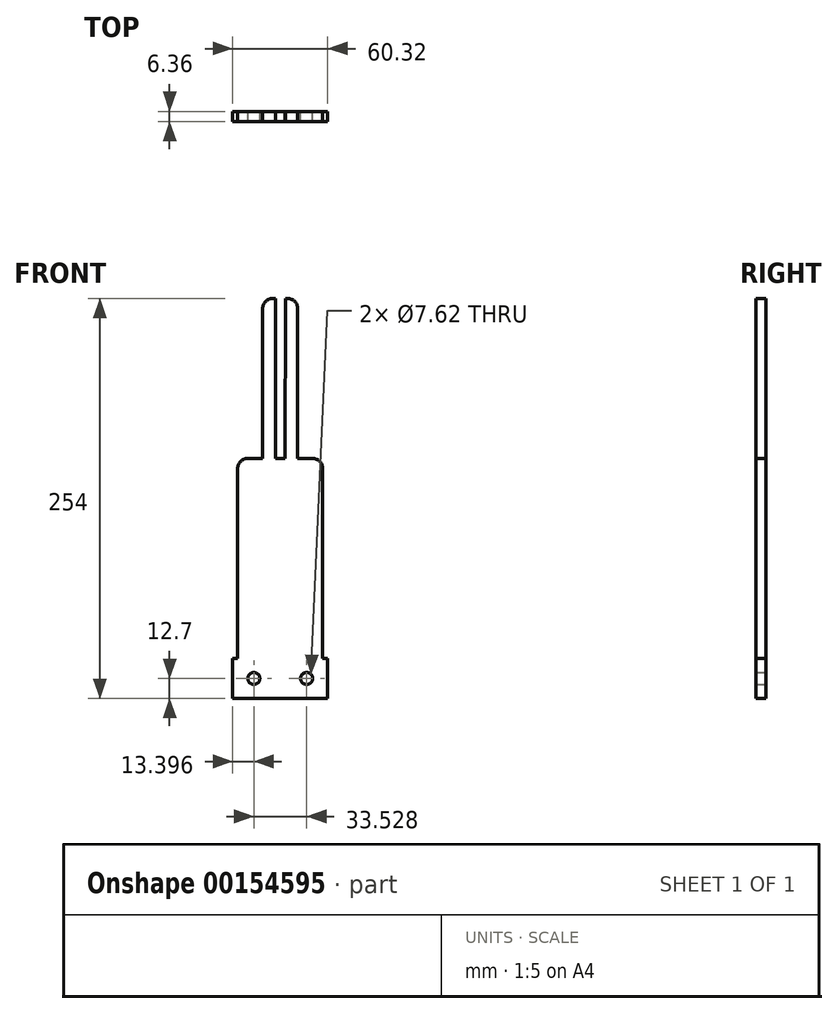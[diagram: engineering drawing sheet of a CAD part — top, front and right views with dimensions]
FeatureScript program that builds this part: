
annotation { "Feature Type Name" : "Feature", "Feature Type Description" : "" }
export const myFeature = defineFeature(function(context is Context, id is Id, definition is map)
    precondition{}
    {
        {
            var Q0;
            Q0=qCreatedBy(makeId("Front.planeOp"),FACE);
            var sketch = newSketch(context, id + "F0", { "sketchPlane" : qUnion([Q0])});
            skLineSegment(sketch, "E0.top", {"start": v(26.99, -12.7) * mm, "end": v(-26.99, -12.7) * mm});
            skLineSegment(sketch, "E0.left", {"start": v(26.99, 133.35) * mm, "end": v(26.99, 12.7) * mm});
            skLineSegment(sketch, "E0.right", {"start": v(-26.99, 133.35) * mm, "end": v(-26.99, 12.7) * mm});
            skPoint(sketch, "E0.middle", {"position": v(0, 0) * mm});
            skLineSegment(sketch, "E1", {"start": v(0, 0) * mm, "end": v(0, -12.7) * mm});
            skLineSegment(sketch, "E2", {"start": v(-20.64, 139.7) * mm, "end": v(-11.11, 139.7) * mm});
            skLineSegment(sketch, "E3", {"start": v(-4.76, 241.3) * mm, "end": v(-3.14, 241.3) * mm});
            skLineSegment(sketch, "E4", {"start": v(11.11, 234.95) * mm, "end": v(11.11, 139.7) * mm});
            skLineSegment(sketch, "E5.trimOffspring", {"start": v(-11.11, 139.7) * mm, "end": v(-11.11, 234.95) * mm});
            skLineSegment(sketch, "E6.trimOffspring", {"start": v(-3.14, 139.7) * mm, "end": v(3.17, 139.7) * mm});
            skLineSegment(sketch, "E7.trimOffspring", {"start": v(11.11, 139.7) * mm, "end": v(20.64, 139.7) * mm});
            skLineSegment(sketch, "E8", {"start": v(-3.14, 139.7) * mm, "end": v(-3.14, 241.3) * mm});
            skLineSegment(sketch, "E9", {"start": v(3.2, 241.3) * mm, "end": v(3.17, 139.7) * mm});
            skLineSegment(sketch, "E10.trimOffspring", {"start": v(3.2, 241.3) * mm, "end": v(4.76, 241.3) * mm});
            skPoint(sketch, "E11.visualSharp", {"position": v(-11.11, 241.3) * mm});
            skArc(sketch, "E11.filletArc", {"start": v(-4.76, 241.3) * mm, "mid": v(-9.25, 239.44) * mm, "end": v(-11.11, 234.95) * mm});
            skPoint(sketch, "E12.visualSharp", {"position": v(11.11, 241.3) * mm});
            skArc(sketch, "E12.filletArc", {"start": v(11.11, 234.95) * mm, "mid": v(9.25, 239.44) * mm, "end": v(4.76, 241.3) * mm});
            skCircle(sketch, "E13", {"center": v(-16.76, 0) * mm, "radius": 3.81 * mm});
            skCircle(sketch, "E14", {"center": v(16.76, 0) * mm, "radius": 3.81 * mm});
            skLineSegment(sketch, "E15", {"start": v(0, -12.7) * mm, "end": v(-3.17, -12.7) * mm});
            skLineSegment(sketch, "E16", {"start": v(-3.17, -12.7) * mm, "end": v(-3.17, 14.57) * mm, "construction": true});
            skLineSegment(sketch, "E17.MirrorCS", {"start": v(3.17, -12.7) * mm, "end": v(3.17, 14.57) * mm, "construction": true});
            skPoint(sketch, "E18.orphan", {"position": v(-26.99, 12.7) * mm});
            skPoint(sketch, "E19.orphan", {"position": v(26.99, 12.7) * mm});
            skLineSegment(sketch, "E20", {"start": v(-26.99, 12.7) * mm, "end": v(-30.16, 12.7) * mm});
            skLineSegment(sketch, "E21", {"start": v(-30.16, 12.7) * mm, "end": v(-30.16, -12.7) * mm});
            skLineSegment(sketch, "E22", {"start": v(-30.16, -12.7) * mm, "end": v(-26.99, -12.7) * mm});
            skLineSegment(sketch, "E23", {"start": v(26.99, -12.7) * mm, "end": v(30.16, -12.7) * mm});
            skLineSegment(sketch, "E24", {"start": v(30.16, -12.7) * mm, "end": v(30.16, 12.7) * mm});
            skLineSegment(sketch, "E25", {"start": v(30.16, 12.7) * mm, "end": v(26.99, 12.7) * mm});
            skPoint(sketch, "E26.visualSharp", {"position": v(-26.99, 139.7) * mm});
            skArc(sketch, "E26.filletArc", {"start": v(-20.64, 139.7) * mm, "mid": v(-25.13, 137.84) * mm, "end": v(-26.99, 133.35) * mm});
            skPoint(sketch, "E27.visualSharp", {"position": v(26.99, 139.7) * mm});
            skArc(sketch, "E27.filletArc", {"start": v(26.99, 133.35) * mm, "mid": v(25.13, 137.84) * mm, "end": v(20.64, 139.7) * mm});
            skSolve(sketch);
        }
        {
            var Q0;
            Q0=qSketchRegion(id+"F0",true);
            extrude(context, id + "F1", {"entities" : qUnion([Q0]), "endBound" : BoundingType.SYMMETRIC, "depth" : 6.35 * mm});
        }
    });
